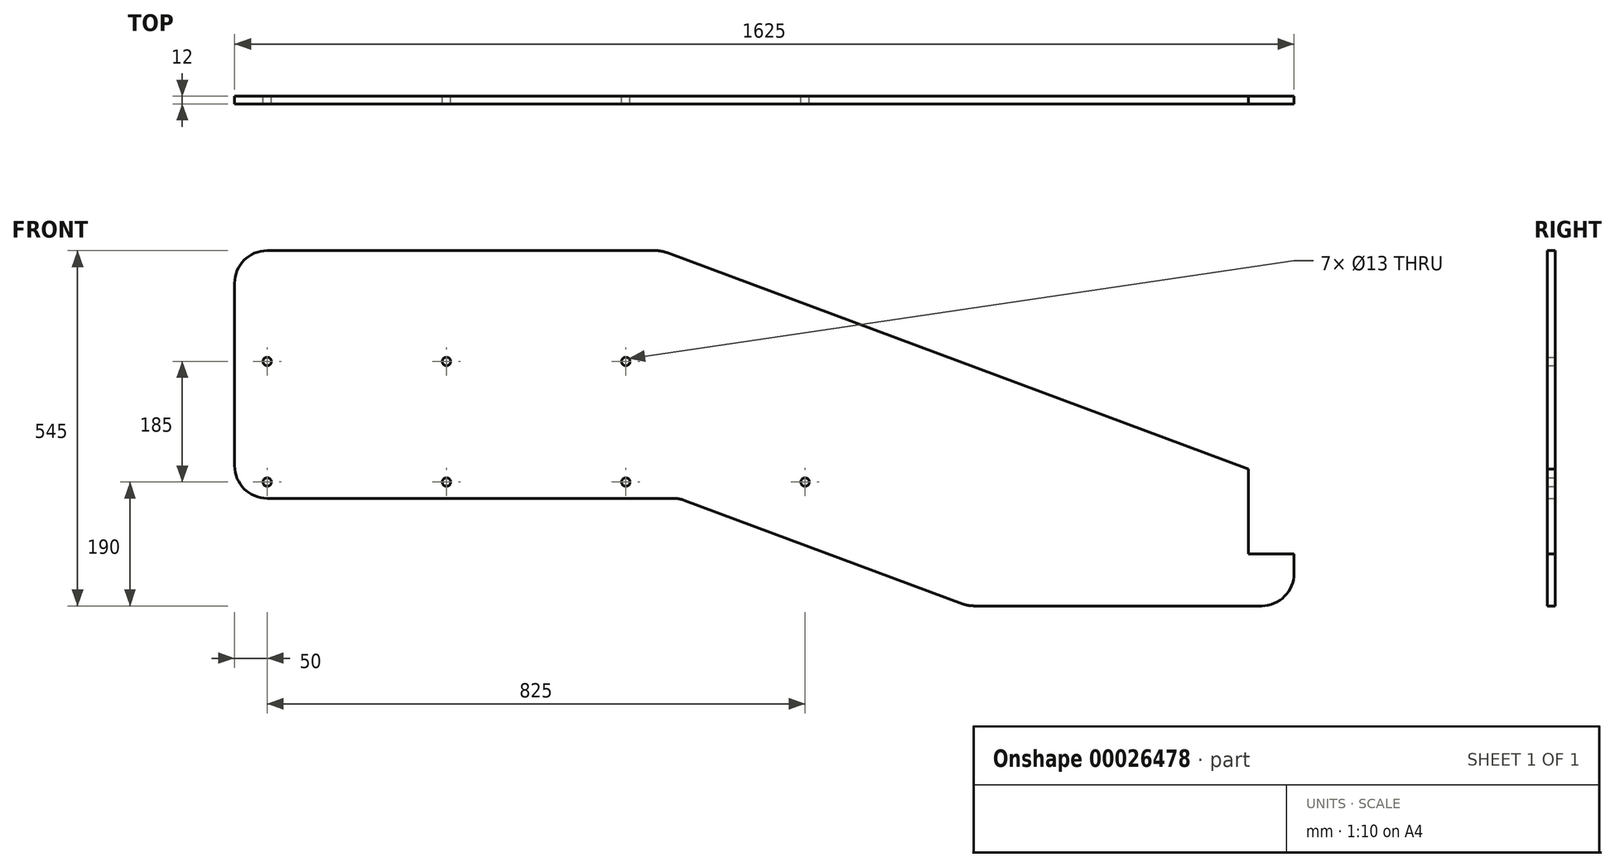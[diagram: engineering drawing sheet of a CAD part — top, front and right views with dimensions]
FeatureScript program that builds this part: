
annotation { "Feature Type Name" : "Feature", "Feature Type Description" : "" }
export const myFeature = defineFeature(function(context is Context, id is Id, definition is map)
    precondition{}
    {
        {
            var Q0;
            Q0=qCreatedBy(makeId("Front.planeOp"),FACE);
            var sketch = newSketch(context, id + "F0", { "sketchPlane" : qUnion([Q0])});
            skLineSegment(sketch, "E0", {"start": v(50, 0) * mm, "end": v(646, 0) * mm});
            skLineSegment(sketch, "E1", {"start": v(0, -50) * mm, "end": v(0, -330) * mm});
            skLineSegment(sketch, "E2", {"start": v(50, -380) * mm, "end": v(672.71, -380) * mm});
            skLineSegment(sketch, "E3", {"start": v(690.15, -383.14) * mm, "end": v(1116.56, -541.86) * mm});
            skLineSegment(sketch, "E4", {"start": v(1134, -545) * mm, "end": v(1575, -545) * mm});
            skLineSegment(sketch, "E5", {"start": v(1625, -495) * mm, "end": v(1625, -465) * mm});
            skLineSegment(sketch, "E6", {"start": v(1625, -465) * mm, "end": v(1555, -465) * mm});
            skLineSegment(sketch, "E7", {"start": v(1555, -465) * mm, "end": v(1555, -335) * mm});
            skLineSegment(sketch, "E8", {"start": v(1555, -335) * mm, "end": v(663.44, -3.14) * mm});
            skCircle(sketch, "E9", {"center": v(50, -170) * mm, "radius": 6.5 * mm});
            skCircle(sketch, "E10", {"center": v(325, -170) * mm, "radius": 6.5 * mm});
            skCircle(sketch, "E11", {"center": v(600, -170) * mm, "radius": 6.5 * mm});
            skCircle(sketch, "E12", {"center": v(50, -355) * mm, "radius": 6.5 * mm});
            skCircle(sketch, "E13", {"center": v(325, -355) * mm, "radius": 6.5 * mm});
            skCircle(sketch, "E14", {"center": v(600, -355) * mm, "radius": 6.5 * mm});
            skCircle(sketch, "E15", {"center": v(875, -355) * mm, "radius": 6.5 * mm});
            skLineSegment(sketch, "E16", {"start": v(50, -355) * mm, "end": v(325, -355) * mm, "construction": true});
            skLineSegment(sketch, "E17", {"start": v(600, -355) * mm, "end": v(325, -355) * mm, "construction": true});
            skLineSegment(sketch, "E18", {"start": v(875, -355) * mm, "end": v(600, -355) * mm, "construction": true});
            skPoint(sketch, "E19.visualSharp", {"position": v(0, 0) * mm});
            skArc(sketch, "E19.filletArc", {"start": v(50, 0) * mm, "mid": v(14.64, -14.64) * mm, "end": v(0, -50) * mm});
            skPoint(sketch, "E20.visualSharp", {"position": v(0, -380) * mm});
            skArc(sketch, "E20.filletArc", {"start": v(0, -330) * mm, "mid": v(14.64, -365.36) * mm, "end": v(50, -380) * mm});
            skPoint(sketch, "E21.visualSharp", {"position": v(681.72, -380) * mm});
            skArc(sketch, "E21.filletArc", {"start": v(690.15, -383.14) * mm, "mid": v(681.57, -380.8) * mm, "end": v(672.71, -380) * mm});
            skPoint(sketch, "E22.visualSharp", {"position": v(1125, -545) * mm});
            skArc(sketch, "E22.filletArc", {"start": v(1116.56, -541.86) * mm, "mid": v(1125.14, -544.2) * mm, "end": v(1134, -545) * mm});
            skPoint(sketch, "E23.visualSharp", {"position": v(1625, -545) * mm});
            skArc(sketch, "E23.filletArc", {"start": v(1575, -545) * mm, "mid": v(1610.36, -530.36) * mm, "end": v(1625, -495) * mm});
            skPoint(sketch, "E24.visualSharp", {"position": v(655, 0) * mm});
            skArc(sketch, "E24.filletArc", {"start": v(663.44, -3.14) * mm, "mid": v(654.86, -0.8) * mm, "end": v(646, 0) * mm});
            skSolve(sketch);
        }
        {
            var Q0;
            Q0=makeQuery(id+"F0.imprint","IMPRINT",FACE,{"disambiguationData":[TD([[makeQuery(id+"F0.imprint","IMPRINT",EDGE,{"derivedFrom":sQuery(id+"F0.wireOp",EDGE,"E0")}),-1.0]])]});
            extrude(context, id + "F1", {"entities" : qUnion([Q0]), "depth" : 12 * mm});
        }
    });
